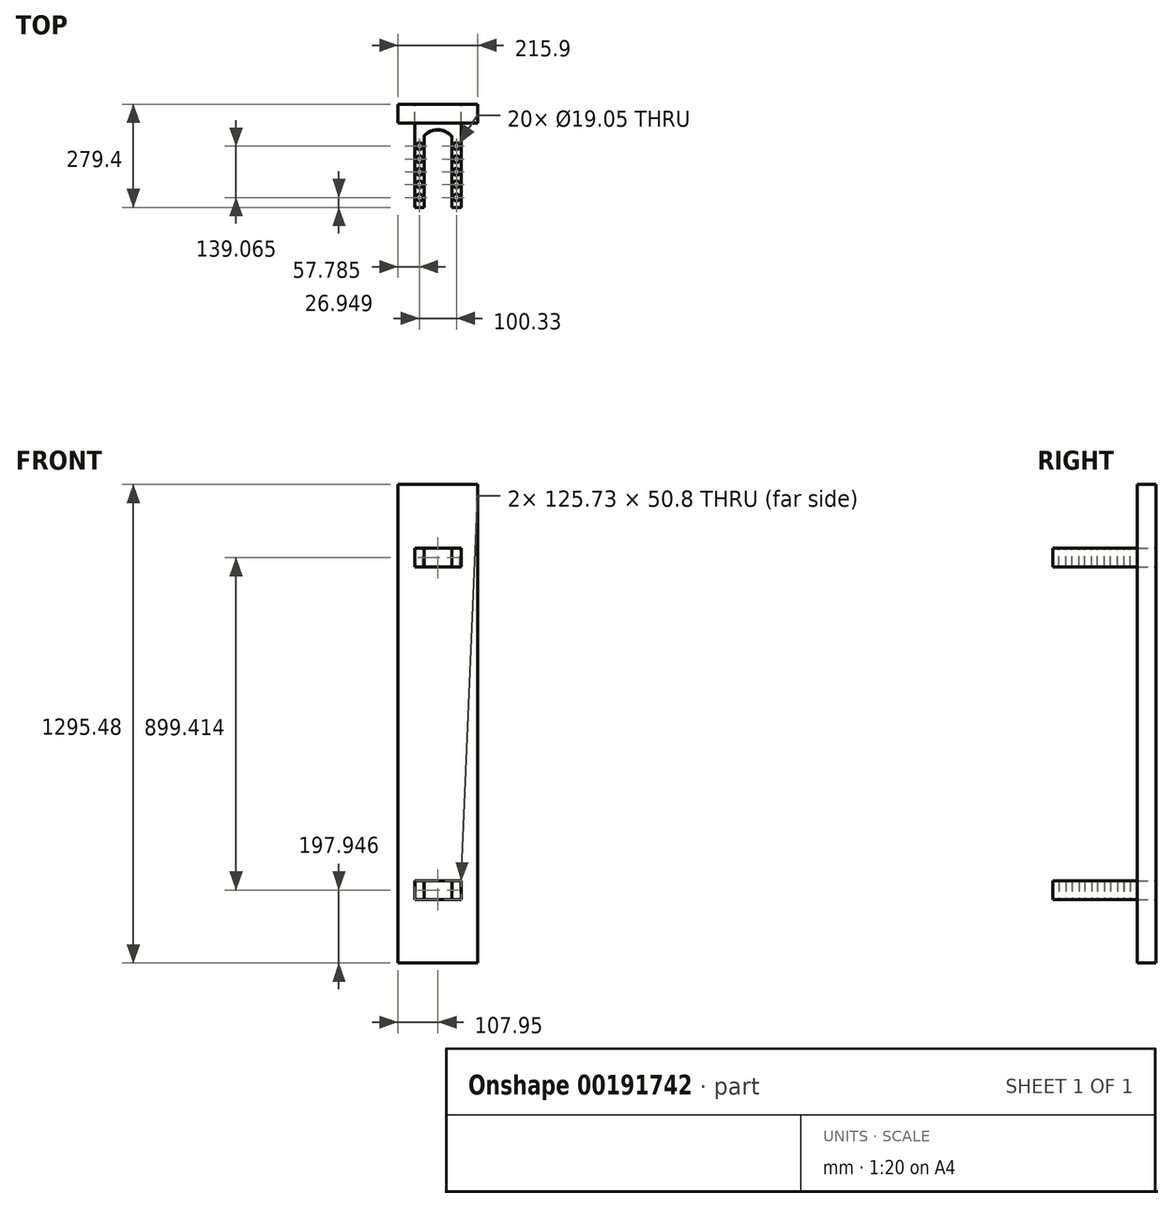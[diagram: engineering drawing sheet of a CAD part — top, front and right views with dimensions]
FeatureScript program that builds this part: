
annotation { "Feature Type Name" : "Feature", "Feature Type Description" : "" }
export const myFeature = defineFeature(function(context is Context, id is Id, definition is map)
    precondition{}
    {
        {
            var Q0;
            Q0=qCreatedBy(makeId("Front.planeOp"),FACE);
            var sketch = newSketch(context, id + "F0", { "sketchPlane" : qUnion([Q0])});
            skLineSegment(sketch, "E0.bottom", {"start": v(-170.82, 172.72) * mm, "end": v(-45.09, 172.72) * mm});
            skLineSegment(sketch, "E0.top", {"start": v(-170.81, -1122.68) * mm, "end": v(-45.08, -1122.68) * mm});
            skLineSegment(sketch, "E0.left", {"start": v(-170.82, 172.72) * mm, "end": v(-170.81, -1122.68) * mm});
            skLineSegment(sketch, "E0.right", {"start": v(-45.09, 172.72) * mm, "end": v(-45.08, -1122.68) * mm});
            skLineSegment(sketch, "E1.bottom", {"start": v(-170.82, 0) * mm, "end": v(-45.09, 0) * mm});
            skLineSegment(sketch, "E1.top", {"start": v(-170.82, -50.8) * mm, "end": v(-45.09, -50.8) * mm});
            skLineSegment(sketch, "E1.left", {"start": v(-170.82, 0) * mm, "end": v(-170.82, -50.8) * mm});
            skLineSegment(sketch, "E1.right", {"start": v(-45.09, 0) * mm, "end": v(-45.09, -50.8) * mm});
            skLineSegment(sketch, "E2.bottom", {"start": v(-170.81, -899.41) * mm, "end": v(-45.08, -899.41) * mm});
            skLineSegment(sketch, "E2.top", {"start": v(-170.81, -950.21) * mm, "end": v(-45.08, -950.21) * mm});
            skLineSegment(sketch, "E2.left", {"start": v(-170.81, -899.41) * mm, "end": v(-170.81, -950.21) * mm});
            skLineSegment(sketch, "E2.right", {"start": v(-45.08, -899.41) * mm, "end": v(-45.08, -950.21) * mm});
            skLineSegment(sketch, "E3.bottom", {"start": v(-45.09, 172.72) * mm, "end": v(0, 172.72) * mm});
            skLineSegment(sketch, "E3.top", {"start": v(-45.08, -1122.76) * mm, "end": v(0, -1122.76) * mm});
            skLineSegment(sketch, "E3.left", {"start": v(-45.09, 172.72) * mm, "end": v(-45.08, -1122.76) * mm});
            skLineSegment(sketch, "E3.right", {"start": v(0, 172.72) * mm, "end": v(0, -1122.76) * mm});
            skLineSegment(sketch, "E4.bottom", {"start": v(-170.82, 172.72) * mm, "end": v(-215.9, 172.72) * mm});
            skLineSegment(sketch, "E4.top", {"start": v(-170.81, -1122.68) * mm, "end": v(-215.9, -1122.68) * mm});
            skLineSegment(sketch, "E4.right", {"start": v(-215.9, 172.72) * mm, "end": v(-215.9, -1122.68) * mm});
            skSolve(sketch);
        }
        {
            var Q0;
            {var subQ0=sQuery(id+"F0.wireOp",EDGE,"E0.bottom");Q0=makeQuery(id+"F0.imprint","IMPRINT",FACE,{"disambiguationData":[TD([[makeQuery(id+"F0.imprint","IMPRINT",EDGE,{"derivedFrom":subQ0}),-1.0]])]});}
            var Q1;
            {var subQ0=sQuery(id+"F0.wireOp",EDGE,"E1.top");Q1=makeQuery(id+"F0.imprint","IMPRINT",FACE,{"disambiguationData":[TD([[makeQuery(id+"F0.imprint","IMPRINT",EDGE,{"derivedFrom":subQ0}),-1.0]])]});}
            var Q2;
            {var subQ0=sQuery(id+"F0.wireOp",EDGE,"E0.top");Q2=makeQuery(id+"F0.imprint","IMPRINT",FACE,{"disambiguationData":[TD([[makeQuery(id+"F0.imprint","IMPRINT",EDGE,{"derivedFrom":subQ0}),1.0]])]});}
            var Q3;
            {var subQ3=sQuery(id+"F0.wireOp",EDGE,"E4.bottom");Q3=makeQuery(id+"F0.imprint","IMPRINT",FACE,{"disambiguationData":[TD([[makeQuery(id+"F0.imprint","IMPRINT",EDGE,{"derivedFrom":subQ3}),1.0]])]});}
            var Q4;
            {var subQ3=sQuery(id+"F0.wireOp",EDGE,"E3.bottom");Q4=makeQuery(id+"F0.imprint","IMPRINT",FACE,{"disambiguationData":[TD([[makeQuery(id+"F0.imprint","IMPRINT",EDGE,{"derivedFrom":subQ3}),-1.0]])]});}
            extrude(context, id + "F1", {"entities" : qUnion([Q0, Q1, Q2, Q3, Q4]), "depth" : 50.8 * mm});
        }
        {
            var Q0;
            Q0=makeQuery(id+"F0.imprint","IMPRINT",FACE,{"disambiguationData":[TD([[makeQuery(id+"F0.imprint","IMPRINT",EDGE,{"derivedFrom":sQuery(id+"F0.wireOp",EDGE,"E1.bottom")}),-1.0]])]});
            var Q1;
            Q1=makeQuery(id+"F0.imprint","IMPRINT",FACE,{"disambiguationData":[TD([[makeQuery(id+"F0.imprint","IMPRINT",EDGE,{"derivedFrom":sQuery(id+"F0.wireOp",EDGE,"E2.bottom")}),-1.0]])]});
            extrude(context, id + "F2", {"entities" : qUnion([Q0, Q1]), "depth" : 279.4 * mm});
        }
        {
            var Q0;
            Q0=makeQuery(id+"F2.opExtrude","SWEPT_FACE",FACE,{"disambiguationData":[OSD([sQuery(id+"F0.wireOp",EDGE,"E2.top")])]});
            var sketch = newSketch(context, id + "F3", { "sketchPlane" : qUnion([Q0])});
            skPoint(sketch, "E5.centerSnap0", {"position": v(-170.82, 139.7) * mm});
            skLineSegment(sketch, "E6.top", {"start": v(-70.49, 284.02) * mm, "end": v(-145.42, 284.02) * mm});
            skLineSegment(sketch, "E6.left", {"start": v(-70.49, 87.61) * mm, "end": v(-70.49, 284.02) * mm});
            skLineSegment(sketch, "E6.right", {"start": v(-145.42, 86.15) * mm, "end": v(-145.42, 284.02) * mm});
            skPoint(sketch, "E7.center.orphan", {"position": v(-108.4, 80.95) * mm});
            skArc(sketch, "E8", {"start": v(-145.42, 86.15) * mm, "mid": v(-107.62, 69.8) * mm, "end": v(-70.49, 87.61) * mm});
            skSolve(sketch);
        }
        {
            var Q0;
            {var subQ0=sQuery(id+"F3.wireOp",EDGE,"E6.top");Q0=makeQuery(id+"F3.imprint","IMPRINT",FACE,{"disambiguationData":[TD([[makeQuery(id+"F3.imprint","IMPRINT",EDGE,{"derivedFrom":subQ0}),1.0]])]});}
            var Q1;
            {var subQ0=sQuery(id+"F3.wireOp",EDGE,"E8");Q1=makeQuery(id+"F3.imprint","IMPRINT",FACE,{"disambiguationData":[TD([[makeQuery(id+"F3.imprint","IMPRINT",EDGE,{"derivedFrom":subQ0}),1.0]])]});}
            extrude(context, id + "F4", {"entities" : qUnion([Q0, Q1]), "operationType" : NewBodyOperationType.REMOVE, "oppositeDirection" : true, "depth" : 154.94 * mm});
        }
        {
            var Q0;
            Q0=makeQuery(id+"F2.opExtrude","SWEPT_FACE",FACE,{"disambiguationData":[OSD([sQuery(id+"F0.wireOp",EDGE,"E1.bottom")])]});
            var sketch = newSketch(context, id + "F5", { "sketchPlane" : qUnion([Q0])});
            skLineSegment(sketch, "E9.top", {"start": v(-145.42, -290.9) * mm, "end": v(-70.49, -290.9) * mm});
            skLineSegment(sketch, "E9.left", {"start": v(-145.42, -85.5) * mm, "end": v(-145.42, -290.9) * mm});
            skLineSegment(sketch, "E9.right", {"start": v(-70.49, -86.15) * mm, "end": v(-70.49, -290.9) * mm});
            skArc(sketch, "E10", {"start": v(-70.49, -86.15) * mm, "mid": v(-107.8, -69.1) * mm, "end": v(-145.42, -85.5) * mm});
            skSolve(sketch);
        }
        {
            var Q0;
            Q0=makeQuery(id+"F5.imprint","IMPRINT",FACE,{"disambiguationData":[TD([[makeQuery(id+"F5.imprint","IMPRINT",EDGE,{"derivedFrom":sQuery(id+"F5.wireOp",EDGE,"Md8b5ywH-h3Ja-cEZK-LcTs-VFdAbwwBdiHD")}),1.0]])]});
            var Q1;
            Q1=makeQuery(id+"F5.imprint","IMPRINT",FACE,{"disambiguationData":[TD([[makeQuery(id+"F5.imprint","IMPRINT",EDGE,{"derivedFrom":sQuery(id+"F5.wireOp",EDGE,"0ObwUE7k-0b5n-ydFT-bEmF-grBz2gHVufYU")}),1.0]])]});
            var Q2;
            {var subQ0=sQuery(id+"F5.wireOp",EDGE,"E9.top");Q2=makeQuery(id+"F5.imprint","IMPRINT",FACE,{"disambiguationData":[TD([[makeQuery(id+"F5.imprint","IMPRINT",EDGE,{"derivedFrom":subQ0}),1.0]])]});}
            var Q3;
            {var subQ0=sQuery(id+"F5.wireOp",EDGE,"N6GL7mUv-4AHG-DVro-2qHL-PViy7rN7htsz");Q3=makeQuery(id+"F5.imprint","IMPRINT",FACE,{"disambiguationData":[TD([[makeQuery(id+"F5.imprint","IMPRINT",EDGE,{"derivedFrom":subQ0}),1.0]])]});}
            var Q4;
            {var subQ0=sQuery(id+"F5.wireOp",EDGE,"E10");Q4=makeQuery(id+"F5.imprint","IMPRINT",FACE,{"disambiguationData":[TD([[makeQuery(id+"F5.imprint","IMPRINT",EDGE,{"derivedFrom":subQ0}),1.0]])]});}
            extrude(context, id + "F6", {"entities" : qUnion([Q0, Q1, Q2, Q3, Q4]), "operationType" : NewBodyOperationType.REMOVE, "oppositeDirection" : true, "depth" : 111.76 * mm});
        }
        {
            var Q0;
            Q0=makeQuery(id+"F2.opExtrude","SWEPT_FACE",FACE,{"disambiguationData":[OSD([sQuery(id+"F0.wireOp",EDGE,"E1.bottom")])]});
            var sketch = newSketch(context, id + "F7", { "sketchPlane" : qUnion([Q0])});
            skCircle(sketch, "E11", {"center": v(-57.79, -113.39) * mm, "radius": 9.53 * mm});
            skCircle(sketch, "E12", {"center": v(-57.79, -148.95) * mm, "radius": 9.53 * mm});
            skCircle(sketch, "E13", {"center": v(-57.79, -182.92) * mm, "radius": 9.53 * mm});
            skCircle(sketch, "E14", {"center": v(-57.79, -216.9) * mm, "radius": 9.53 * mm});
            skCircle(sketch, "E15", {"center": v(-57.79, -252.45) * mm, "radius": 9.53 * mm});
            skSolve(sketch);
        }
        {
            var Q0;
            Q0=makeQuery(id+"F7.imprint","IMPRINT",FACE,{"disambiguationData":[TD([[makeQuery(id+"F7.imprint","IMPRINT",EDGE,{"derivedFrom":sQuery(id+"F7.wireOp",EDGE,"E11")}),-1.0]])]});
            var sketch = newSketch(context, id + "F8", { "sketchPlane" : qUnion([Q0])});
            skSolve(sketch);
        }
        {
            var Q0;
            Q0=makeQuery(id+"F7.imprint","IMPRINT",FACE,{"disambiguationData":[TD([[makeQuery(id+"F7.imprint","IMPRINT",EDGE,{"derivedFrom":sQuery(id+"F7.wireOp",EDGE,"E11")}),1.0]])]});
            var Q1;
            Q1=makeQuery(id+"F7.imprint","IMPRINT",FACE,{"disambiguationData":[TD([[makeQuery(id+"F7.imprint","IMPRINT",EDGE,{"derivedFrom":sQuery(id+"F7.wireOp",EDGE,"E12")}),1.0]])]});
            var Q2;
            Q2=makeQuery(id+"F7.imprint","IMPRINT",FACE,{"disambiguationData":[TD([[makeQuery(id+"F7.imprint","IMPRINT",EDGE,{"derivedFrom":sQuery(id+"F7.wireOp",EDGE,"E13")}),1.0]])]});
            var Q3;
            Q3=makeQuery(id+"F7.imprint","IMPRINT",FACE,{"disambiguationData":[TD([[makeQuery(id+"F7.imprint","IMPRINT",EDGE,{"derivedFrom":sQuery(id+"F7.wireOp",EDGE,"2OHANAlA-4pJe-6xW3-kCWq-s1pkgEI0P5xa")}),1.0]])]});
            var Q4;
            Q4=makeQuery(id+"F7.imprint","IMPRINT",FACE,{"disambiguationData":[TD([[makeQuery(id+"F7.imprint","IMPRINT",EDGE,{"derivedFrom":sQuery(id+"F7.wireOp",EDGE,"QpNfSZ5R-XWYB-knRW-UeNi-cyGIBEhZvUf1")}),1.0]])]});
            var Q5;
            Q5=makeQuery(id+"F7.imprint","IMPRINT",FACE,{"disambiguationData":[TD([[makeQuery(id+"F7.imprint","IMPRINT",EDGE,{"derivedFrom":sQuery(id+"F7.wireOp",EDGE,"E15")}),1.0]])]});
            var Q6;
            Q6=makeQuery(id+"F7.imprint","IMPRINT",FACE,{"disambiguationData":[TD([[makeQuery(id+"F7.imprint","IMPRINT",EDGE,{"derivedFrom":sQuery(id+"F7.wireOp",EDGE,"E14")}),1.0]])]});
            extrude(context, id + "F9", {"entities" : qUnion([Q0, Q1, Q2, Q3, Q4, Q5, Q6]), "operationType" : NewBodyOperationType.REMOVE, "oppositeDirection" : true, "depth" : 53.34 * mm});
        }
        {
            var Q0;
            Q0=makeQuery(id+"F8.imprint","IMPRINT",FACE,{"disambiguationData":[TD([[makeQuery(id+"F8.imprint","IMPRINT",EDGE,{"derivedFrom":makeQuery(id+"F7.imprint","IMPRINT",EDGE,{"derivedFrom":sQuery(id+"F7.wireOp",EDGE,"E11")})}),-1.0]])]});
            var sketch = newSketch(context, id + "F10", { "sketchPlane" : qUnion([Q0])});
            skCircle(sketch, "E16", {"center": v(-158.12, -113.39) * mm, "radius": 9.53 * mm});
            skCircle(sketch, "E17", {"center": v(-158.12, -148.95) * mm, "radius": 9.53 * mm});
            skCircle(sketch, "E18", {"center": v(-158.12, -182.92) * mm, "radius": 9.53 * mm});
            skCircle(sketch, "E19", {"center": v(-158.12, -216.9) * mm, "radius": 9.53 * mm});
            skCircle(sketch, "E20", {"center": v(-158.12, -252.45) * mm, "radius": 9.53 * mm});
            skSolve(sketch);
        }
        {
            var Q0;
            Q0 = qSketchRegion(id + "F10", true);
            extrude(context, id + "F11", {"entities" : qUnion([Q0]), "operationType" : NewBodyOperationType.REMOVE, "oppositeDirection" : true, "depth" : 53.34 * mm});
        }
        {
            var Q0;
            Q0=makeQuery(id+"F2.opExtrude","SWEPT_FACE",FACE,{"disambiguationData":[OSD([sQuery(id+"F0.wireOp",EDGE,"E2.top")])]});
            var sketch = newSketch(context, id + "F12", { "sketchPlane" : qUnion([Q0])});
            skCircle(sketch, "E21", {"center": v(-158.12, 113.39) * mm, "radius": 9.53 * mm});
            skCircle(sketch, "E22", {"center": v(-158.12, 148.95) * mm, "radius": 9.53 * mm});
            skCircle(sketch, "E23", {"center": v(-158.12, 182.92) * mm, "radius": 9.53 * mm});
            skCircle(sketch, "E24", {"center": v(-158.12, 216.9) * mm, "radius": 9.53 * mm});
            skCircle(sketch, "E25", {"center": v(-158.12, 252.45) * mm, "radius": 9.53 * mm});
            skCircle(sketch, "E26", {"center": v(-57.79, 113.39) * mm, "radius": 9.53 * mm});
            skCircle(sketch, "E27", {"center": v(-57.79, 148.95) * mm, "radius": 9.53 * mm});
            skCircle(sketch, "E28", {"center": v(-57.79, 182.92) * mm, "radius": 9.53 * mm});
            skCircle(sketch, "E29", {"center": v(-57.79, 216.9) * mm, "radius": 9.53 * mm});
            skCircle(sketch, "E30", {"center": v(-57.79, 252.45) * mm, "radius": 9.53 * mm});
            skSolve(sketch);
        }
        {
            var Q0;
            Q0 = qSketchRegion(id + "F12", true);
            var Q1;
            Q1=makeQuery(id+"F12.imprint","IMPRINT",FACE,{"disambiguationData":[TD([[makeQuery(id+"F12.imprint","IMPRINT",EDGE,{"derivedFrom":sQuery(id+"F12.wireOp",EDGE,"E26")}),1.0]])]});
            extrude(context, id + "F13", {"entities" : qUnion([Q0, Q1]), "operationType" : NewBodyOperationType.REMOVE, "oppositeDirection" : true, "depth" : 53.34 * mm});
        }
    });
